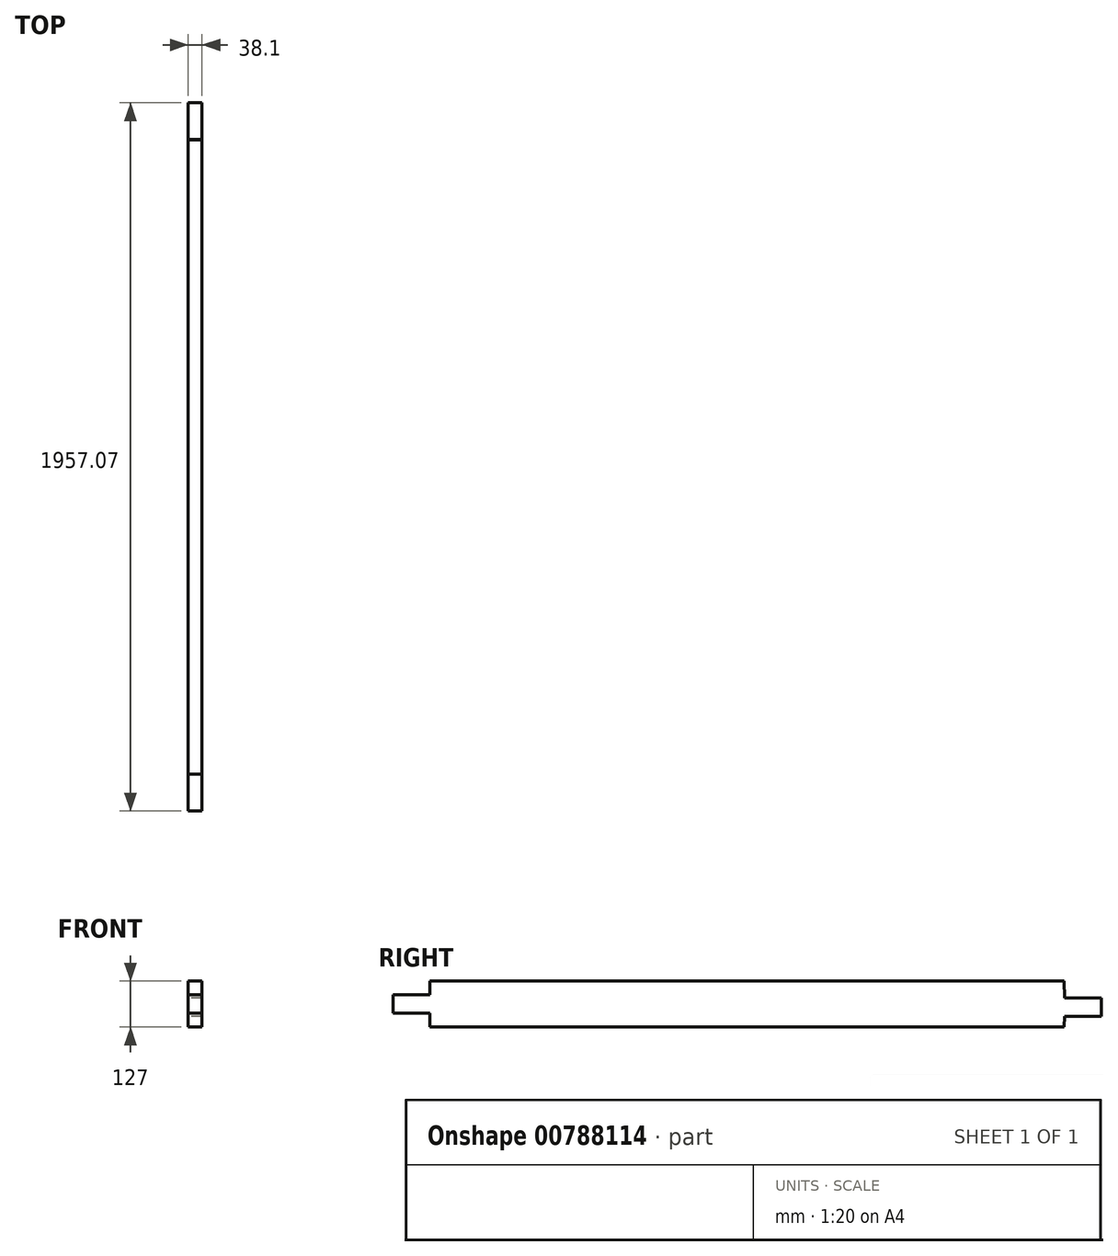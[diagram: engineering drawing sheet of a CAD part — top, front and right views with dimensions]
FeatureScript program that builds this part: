
annotation { "Feature Type Name" : "Feature", "Feature Type Description" : "" }
export const myFeature = defineFeature(function(context is Context, id is Id, definition is map)
    precondition{}
    {
        {
            var Q0;
            Q0=qCreatedBy(makeId("Right.planeOp"),FACE);
            var sketch = newSketch(context, id + "F0", { "sketchPlane" : qUnion([Q0])});
            skLineSegment(sketch, "E0", {"start": v(-1816.27, 67.07) * mm, "end": v(-1714.67, 67.07) * mm});
            skLineSegment(sketch, "E1", {"start": v(-1714.67, 67.07) * mm, "end": v(-1714.67, 105.17) * mm});
            skLineSegment(sketch, "E2", {"start": v(-1816.27, 16.27) * mm, "end": v(-1714.67, 16.27) * mm});
            skLineSegment(sketch, "E3", {"start": v(-1714.67, 16.27) * mm, "end": v(-1714.67, -21.83) * mm});
            skLineSegment(sketch, "E4", {"start": v(140.8, 58.19) * mm, "end": v(39.2, 58.19) * mm});
            skLineSegment(sketch, "E5", {"start": v(39.2, 58.19) * mm, "end": v(37.93, 105.17) * mm});
            skLineSegment(sketch, "E6", {"start": v(140.8, 7.39) * mm, "end": v(39.2, 7.39) * mm});
            skLineSegment(sketch, "E7", {"start": v(39.2, 7.39) * mm, "end": v(37.93, -21.83) * mm});
            skLineSegment(sketch, "E8", {"start": v(140.8, 58.19) * mm, "end": v(140.8, 7.39) * mm});
            skLineSegment(sketch, "E9", {"start": v(37.93, -21.83) * mm, "end": v(-1714.67, -21.83) * mm});
            skLineSegment(sketch, "E10", {"start": v(-1714.67, 105.17) * mm, "end": v(37.93, 105.17) * mm});
            skLineSegment(sketch, "E11", {"start": v(-1816.27, 67.07) * mm, "end": v(-1816.27, 16.27) * mm});
            skLineSegment(sketch, "E12", {"start": v(-1714.67, 67.07) * mm, "end": v(-1714.67, 16.27) * mm});
            skLineSegment(sketch, "E13", {"start": v(39.2, 7.39) * mm, "end": v(39.2, 58.19) * mm});
            skSolve(sketch);
        }
        {
            var Q0;
            Q0=makeQuery(id+"F0.imprint","IMPRINT",FACE,{"disambiguationData":[TD([[makeQuery(id+"F0.imprint","IMPRINT",EDGE,{"derivedFrom":sQuery(id+"F0.wireOp",EDGE,"E1")}),-1.0]])]});
            extrude(context, id + "F1", {"entities" : qUnion([Q0]), "endBound" : BoundingType.SYMMETRIC, "depth" : 38.1 * mm, "offsetDistance" : 25.4 * mm});
        }
        {
            var Q0;
            Q0=makeQuery(id+"F0.imprint","IMPRINT",FACE,{"disambiguationData":[TD([[makeQuery(id+"F0.imprint","IMPRINT",EDGE,{"derivedFrom":sQuery(id+"F0.wireOp",EDGE,"E4")}),1.0]])]});
            var Q1;
            Q1=makeQuery(id+"F0.imprint","IMPRINT",FACE,{"disambiguationData":[TD([[makeQuery(id+"F0.imprint","IMPRINT",EDGE,{"derivedFrom":sQuery(id+"F0.wireOp",EDGE,"E0")}),-1.0]])]});
            extrude(context, id + "F2", {"entities" : qUnion([Q0, Q1]), "operationType" : NewBodyOperationType.ADD, "endBound" : BoundingType.SYMMETRIC, "depth" : 38.1 * mm, "offsetDistance" : 25.4 * mm});
        }
    });
